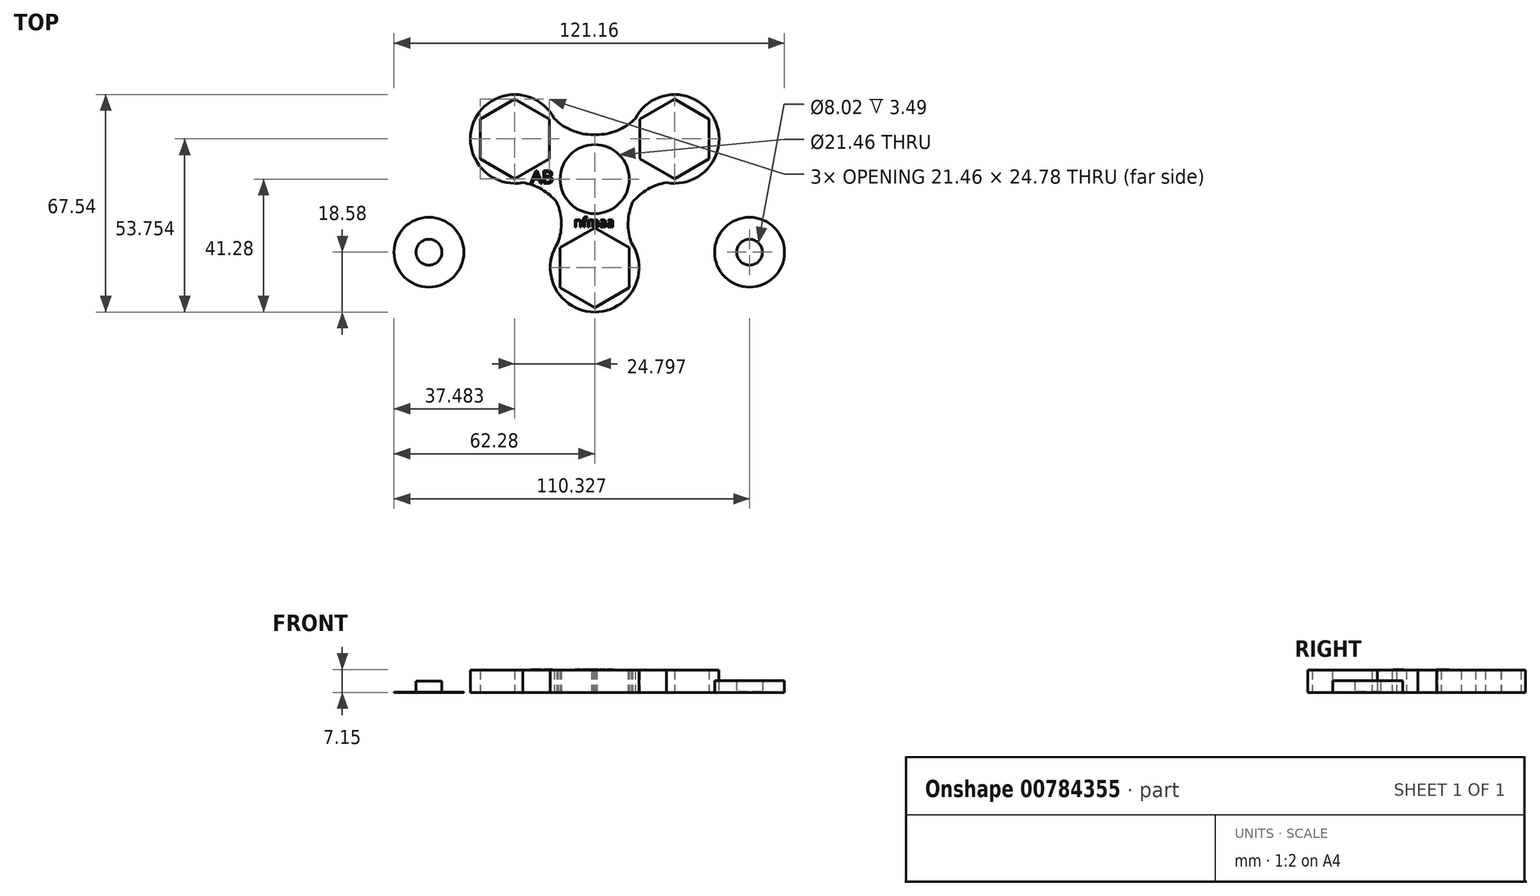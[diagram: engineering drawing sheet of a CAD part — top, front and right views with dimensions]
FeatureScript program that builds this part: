
annotation { "Feature Type Name" : "Feature", "Feature Type Description" : "" }
export const myFeature = defineFeature(function(context is Context, id is Id, definition is map)
    precondition{}
    {
        {
            var Q0;
            Q0=qCreatedBy(makeId("Top.planeOp"),FACE);
            var sketch = newSketch(context, id + "F0", { "sketchPlane" : qUnion([Q0])});
            skCircle(sketch, "E0", {"center": v(0, 0) * mm, "radius": 10.73 * mm});
            skCircle(sketch, "E1", {"center": v(0, 0) * mm, "radius": 13.78 * mm});
            skCircle(sketch, "E2", {"center": v(-24.8, 12.47) * mm, "radius": 13.78 * mm});
            skCircle(sketch, "E3", {"center": v(24.8, 12.47) * mm, "radius": 13.78 * mm});
            skCircle(sketch, "E4", {"center": v(0, -27.5) * mm, "radius": 13.78 * mm});
            skArc(sketch, "E5", {"start": v(-15.38, 22.53) * mm, "mid": v(-8.9, 16.01) * mm, "end": v(0, 13.78) * mm});
            skArc(sketch, "E6.MirrorCS", {"start": v(15.38, 22.53) * mm, "mid": v(8.9, 16.01) * mm, "end": v(0, 13.78) * mm});
            skPoint(sketch, "E7", {"position": v(11.77, -7.16) * mm});
            skArc(sketch, "E8", {"start": v(27.47, -1.05) * mm, "mid": v(18.81, -2.04) * mm, "end": v(11.77, -7.16) * mm});
            skArc(sketch, "E9.MirrorCS", {"start": v(-27.47, -1.05) * mm, "mid": v(-18.81, -2.04) * mm, "end": v(-11.77, -7.16) * mm});
            skArc(sketch, "E10", {"start": v(11.77, -7.16) * mm, "mid": v(10.42, -15.39) * mm, "end": v(13.12, -23.27) * mm});
            skArc(sketch, "E11.MirrorCS", {"start": v(-11.77, -7.16) * mm, "mid": v(-10.42, -15.39) * mm, "end": v(-13.12, -23.27) * mm});
            skLineSegment(sketch, "E12.0", {"start": v(-14.07, 18.67) * mm, "end": v(-14.07, 6.28) * mm});
            skLineSegment(sketch, "E12.1", {"start": v(-14.07, 6.28) * mm, "end": v(-24.8, 0.08) * mm});
            skLineSegment(sketch, "E12.2", {"start": v(-24.8, 0.08) * mm, "end": v(-35.53, 6.28) * mm});
            skLineSegment(sketch, "E12.3", {"start": v(-35.53, 6.28) * mm, "end": v(-35.53, 18.67) * mm});
            skLineSegment(sketch, "E12.4", {"start": v(-35.53, 18.67) * mm, "end": v(-24.8, 24.86) * mm});
            skLineSegment(sketch, "E12.5", {"start": v(-24.8, 24.86) * mm, "end": v(-14.07, 18.67) * mm});
            skLineSegment(sketch, "E13.0", {"start": v(14.07, 6.28) * mm, "end": v(14.07, 18.67) * mm});
            skLineSegment(sketch, "E13.1", {"start": v(14.07, 18.67) * mm, "end": v(24.8, 24.86) * mm});
            skLineSegment(sketch, "E13.2", {"start": v(24.8, 24.86) * mm, "end": v(35.53, 18.67) * mm});
            skLineSegment(sketch, "E13.3", {"start": v(35.53, 18.67) * mm, "end": v(35.53, 6.28) * mm});
            skLineSegment(sketch, "E13.4", {"start": v(35.53, 6.28) * mm, "end": v(24.8, 0.08) * mm});
            skLineSegment(sketch, "E13.5", {"start": v(24.8, 0.08) * mm, "end": v(14.07, 6.28) * mm});
            skLineSegment(sketch, "E14.0", {"start": v(10.73, -21.3) * mm, "end": v(10.73, -33.7) * mm});
            skLineSegment(sketch, "E14.1", {"start": v(10.73, -33.7) * mm, "end": v(0, -39.9) * mm});
            skLineSegment(sketch, "E14.2", {"start": v(0, -39.9) * mm, "end": v(-10.73, -33.7) * mm});
            skLineSegment(sketch, "E14.3", {"start": v(-10.73, -33.7) * mm, "end": v(-10.73, -21.3) * mm});
            skLineSegment(sketch, "E14.4", {"start": v(-10.73, -21.3) * mm, "end": v(0, -15.11) * mm});
            skLineSegment(sketch, "E14.5", {"start": v(0, -15.11) * mm, "end": v(10.73, -21.3) * mm});
            skSolve(sketch);
        }
        {
            var Q0;
            Q0 = qSketchRegion(id + "F0", true);
            extrude(context, id + "F1", {"entities" : qUnion([Q0]), "depth" : 7 * mm, "offsetDistance" : 25 * mm});
        }
        {
            var Q0;
            Q0=qCreatedBy(makeId("Top.planeOp"),FACE);
            var sketch = newSketch(context, id + "F2", { "sketchPlane" : qUnion([Q0])});
            skText(sketch, "E15", { "text": "nfmaa", "fontName": "OpenSans-Regular.ttf"});
            skText(sketch, "E16", { "text": "AB", "fontName": "OpenSans-Regular.ttf"});
            const initialGuessF2  = {"E15": [-0.00646, -0.01488, 1, 0, 0.003], "E16": [-0.01985, -0.0013, 1, 0, 0.00394]};
            skSetInitialGuess(sketch, initialGuessF2);
            skSolve(sketch);
        }
        {
            var Q0;
            Q0=qCreatedBy(makeId("Top.planeOp"),FACE);
            var sketch = newSketch(context, id + "F3", { "sketchPlane" : qUnion([Q0])});
            skCircle(sketch, "E17", {"center": v(-51.44, -22.7) * mm, "radius": 4.01 * mm});
            skCircle(sketch, "E18", {"center": v(-51.44, -22.7) * mm, "radius": 10.84 * mm});
            skCircle(sketch, "E19.MirrorC", {"center": v(48.05, -22.7) * mm, "radius": 4.01 * mm});
            skCircle(sketch, "E20.MirrorC", {"center": v(48.05, -22.7) * mm, "radius": 10.84 * mm});
            skSolve(sketch);
        }
        {
            var Q0;
            Q0 = qSketchRegion(id + "F2", true);
            extrude(context, id + "F4", {"entities" : qUnion([Q0]), "operationType" : NewBodyOperationType.ADD, "depth" : 7.15 * mm, "offsetDistance" : 25 * mm});
        }
        {
            var Q0;
            Q0=makeQuery(id+"F3.imprint","IMPRINT",FACE,{"disambiguationData":[TD([[makeQuery(id+"F3.imprint","IMPRINT",EDGE,{"derivedFrom":sQuery(id+"F3.wireOp",EDGE,"E17")}),-1.0]])]});
            extrude(context, id + "F5", {"entities" : qUnion([Q0]), "depth" : 0.1 * mm, "offsetDistance" : 25 * mm});
        }
        {
            var Q0;
            Q0=makeQuery(id+"F3.imprint","IMPRINT",FACE,{"disambiguationData":[TD([[makeQuery(id+"F3.imprint","IMPRINT",EDGE,{"derivedFrom":sQuery(id+"F3.wireOp",EDGE,"E17")}),1.0]])]});
            extrude(context, id + "F6", {"entities" : qUnion([Q0]), "operationType" : NewBodyOperationType.ADD, "depth" : 3.58 * mm, "offsetDistance" : 25 * mm});
        }
        {
            var Q0;
            Q0=makeQuery(id+"F3.imprint","IMPRINT",FACE,{"disambiguationData":[TD([[makeQuery(id+"F3.imprint","IMPRINT",EDGE,{"derivedFrom":sQuery(id+"F3.wireOp",EDGE,"E19.MirrorC")}),1.0]])]});
            extrude(context, id + "F7", {"entities" : qUnion([Q0]), "depth" : 0.2 * mm, "offsetDistance" : 25 * mm});
        }
        {
            var Q0;
            Q0=makeQuery(id+"F3.imprint","IMPRINT",FACE,{"disambiguationData":[TD([[makeQuery(id+"F3.imprint","IMPRINT",EDGE,{"derivedFrom":sQuery(id+"F3.wireOp",EDGE,"E19.MirrorC")}),-1.0]])]});
            extrude(context, id + "F8", {"entities" : qUnion([Q0]), "operationType" : NewBodyOperationType.ADD, "depth" : 3.69 * mm, "offsetDistance" : 25 * mm});
        }
    });
